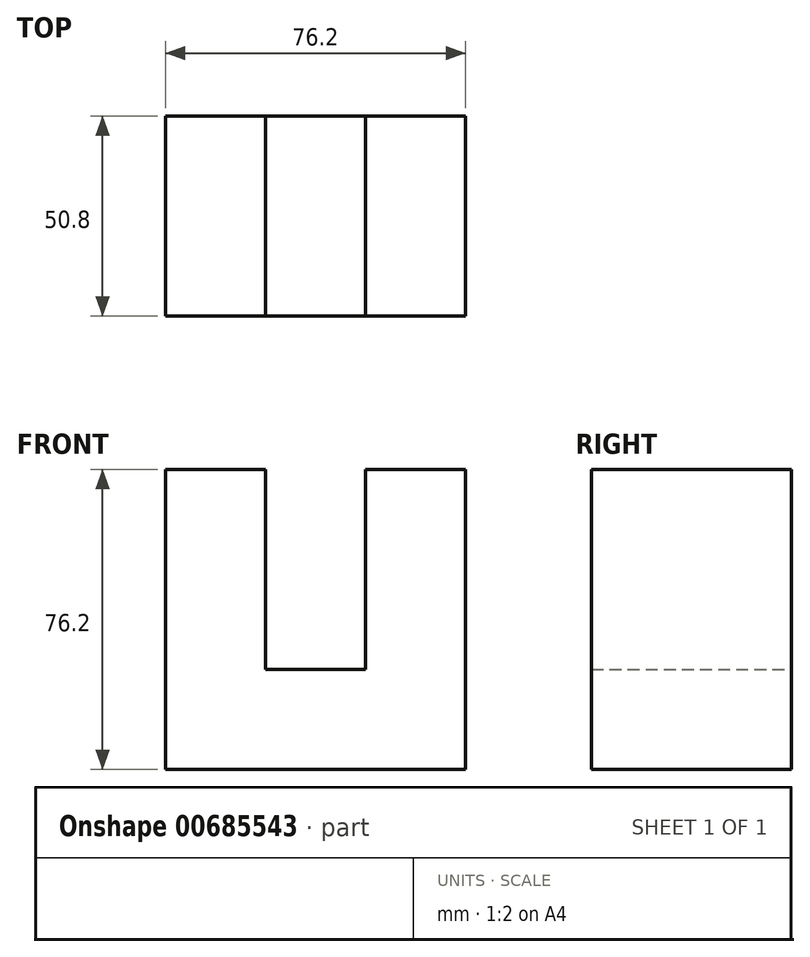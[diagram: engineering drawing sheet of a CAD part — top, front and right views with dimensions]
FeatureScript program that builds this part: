
annotation { "Feature Type Name" : "Feature", "Feature Type Description" : "" }
export const myFeature = defineFeature(function(context is Context, id is Id, definition is map)
    precondition{}
    {
        {
            var Q0;
            Q0=qCreatedBy(makeId("Front.planeOp"),FACE);
            var sketch = newSketch(context, id + "F0", { "sketchPlane" : qUnion([Q0])});
            skLineSegment(sketch, "E0", {"start": v(0, 0) * mm, "end": v(-76.2, 0) * mm});
            skLineSegment(sketch, "E1", {"start": v(-76.2, 0) * mm, "end": v(-76.2, 76.2) * mm});
            skLineSegment(sketch, "E2", {"start": v(-76.2, 76.2) * mm, "end": v(-50.8, 76.2) * mm});
            skLineSegment(sketch, "E3", {"start": v(-50.8, 76.2) * mm, "end": v(-50.8, 25.4) * mm});
            skLineSegment(sketch, "E4", {"start": v(-50.8, 25.4) * mm, "end": v(-25.4, 25.4) * mm});
            skLineSegment(sketch, "E5", {"start": v(-25.4, 25.4) * mm, "end": v(-25.4, 76.2) * mm});
            skLineSegment(sketch, "E6", {"start": v(-25.4, 76.2) * mm, "end": v(0, 76.2) * mm});
            skLineSegment(sketch, "E7", {"start": v(0, 76.2) * mm, "end": v(0, 0) * mm});
            skSolve(sketch);
        }
        {
            var Q0;
            Q0=makeQuery(id+"F0.imprint","IMPRINT",FACE,{"disambiguationData":[TD([[makeQuery(id+"F0.imprint","IMPRINT",EDGE,{"derivedFrom":sQuery(id+"F0.wireOp",EDGE,"E0")}),-1.0]])]});
            extrude(context, id + "F1", {"entities" : qUnion([Q0]), "depth" : 50.8 * mm, "offsetDistance" : 25.4 * mm});
        }
    });
